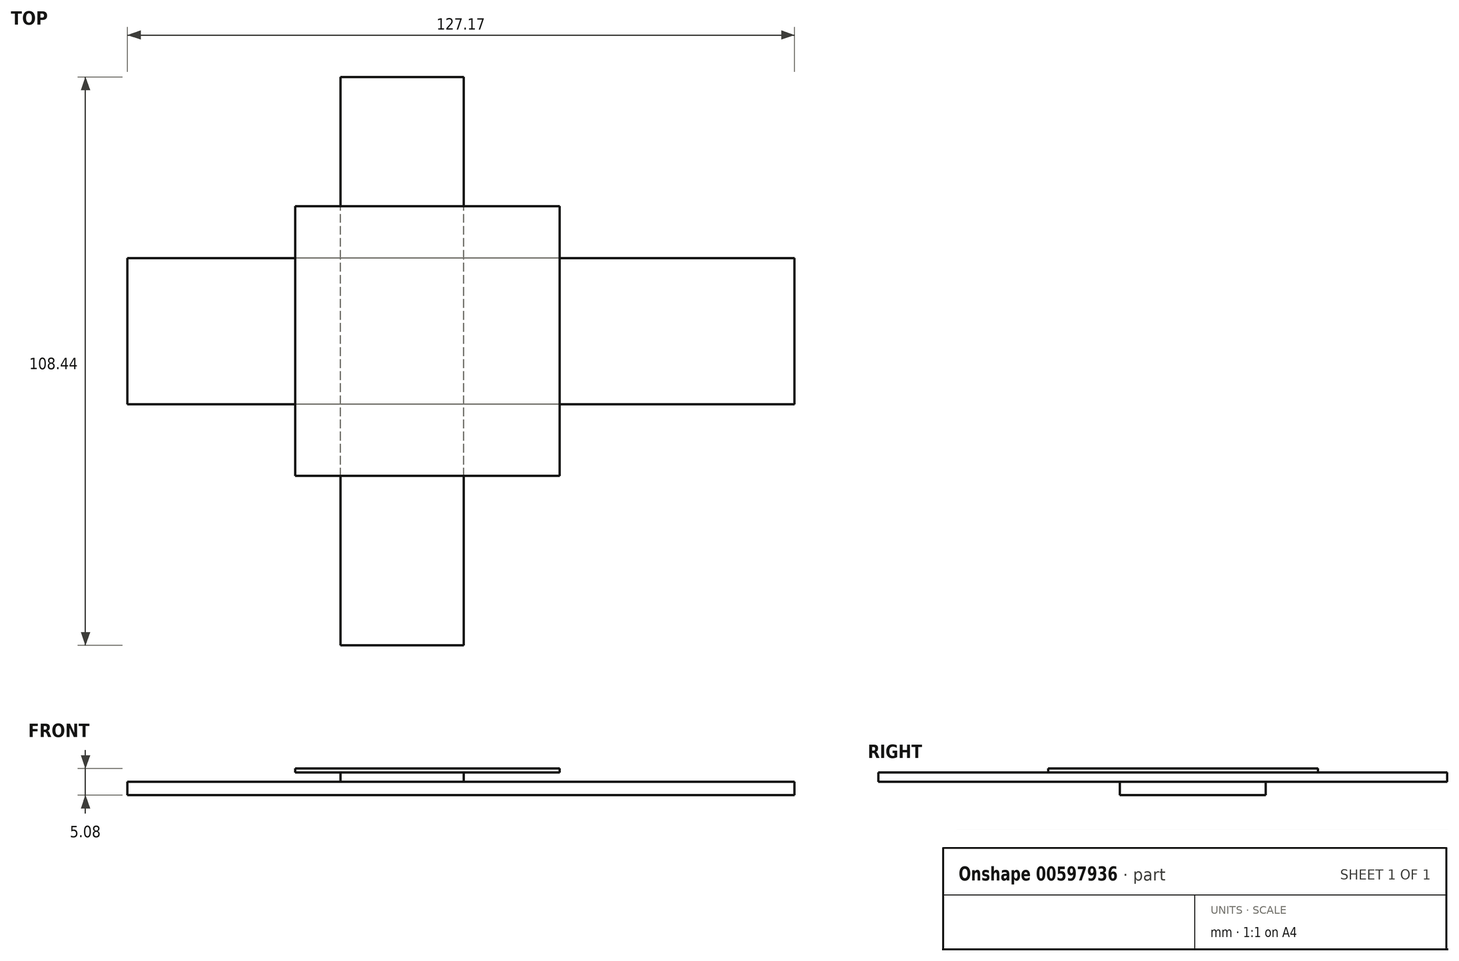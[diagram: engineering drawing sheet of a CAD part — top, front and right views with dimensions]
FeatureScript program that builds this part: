
annotation { "Feature Type Name" : "Feature", "Feature Type Description" : "" }
export const myFeature = defineFeature(function(context is Context, id is Id, definition is map)
    precondition{}
    {
        {
            var Q0;
            Q0=qCreatedBy(makeId("Top.planeOp"),FACE);
            var sketch = newSketch(context, id + "F0", { "sketchPlane" : qUnion([Q0])});
            skLineSegment(sketch, "E0.bottom", {"start": v(49.35, 0) * mm, "end": v(-77.82, 0) * mm});
            skLineSegment(sketch, "E0.top", {"start": v(49.35, 27.86) * mm, "end": v(-77.82, 27.86) * mm});
            skLineSegment(sketch, "E0.left", {"start": v(49.35, 0) * mm, "end": v(49.35, 27.86) * mm});
            skLineSegment(sketch, "E0.right", {"start": v(-77.82, 0) * mm, "end": v(-77.82, 27.86) * mm});
            skPoint(sketch, "E0.middle", {"position": v(-14.24, 13.93) * mm});
            skSolve(sketch);
        }
        {
            var Q0;
            Q0 = qSketchRegion(id + "F0", true);
            extrude(context, id + "F1", {"entities" : qUnion([Q0]), "depth" : 2.54 * mm, "offsetDistance" : 25.4 * mm});
        }
        {
            var Q0;
            Q0=makeQuery(id+"F1.opExtrude","CAP_FACE",FACE,{"disambiguationData":[OSD([sQuery(id+"F0.wireOp",EDGE,"E0.bottom"),sQuery(id+"F0.wireOp",EDGE,"E0.top"),sQuery(id+"F0.wireOp",EDGE,"E0.left"),sQuery(id+"F0.wireOp",EDGE,"E0.right")])],"isStart":false});
            var sketch = newSketch(context, id + "F2", { "sketchPlane" : qUnion([Q0])});
            skLineSegment(sketch, "E1.bottom", {"start": v(-13.68, -46.02) * mm, "end": v(-37.2, -46.02) * mm});
            skLineSegment(sketch, "E1.top", {"start": v(-13.68, 62.42) * mm, "end": v(-37.2, 62.42) * mm});
            skLineSegment(sketch, "E1.left", {"start": v(-13.68, -46.02) * mm, "end": v(-13.68, 62.42) * mm});
            skLineSegment(sketch, "E1.right", {"start": v(-37.2, -46.02) * mm, "end": v(-37.2, 62.42) * mm});
            skPoint(sketch, "E1.middle", {"position": v(-25.43, 8.2) * mm});
            skSolve(sketch);
        }
        {
            var Q0;
            {var subQ0=sQuery(id+"F2.wireOp",EDGE,"E1.left");var subQ1=makeQuery(id+"F1.opExtrude","CAP_EDGE",EDGE,{"disambiguationData":[OSD([sQuery(id+"F0.wireOp",EDGE,"E0.bottom")])],"isStart":false});var subQ2=makeQuery(id+"F2.imprint","INTERSECT",VERTEX,{"derivedFrom":[subQ1,subQ0]});Q0=makeQuery(id+"F2.imprint","IMPRINT",FACE,{"disambiguationData":[TD([[makeQuery(id+"F2.imprint","IMPRINT",EDGE,{"disambiguationData":[TD([[subQ2,-1.0]])],"derivedFrom":subQ0}),1.0]])]});}
            var Q1;
            {var subQ0=sQuery(id+"F2.wireOp",EDGE,"E1.bottom");Q1=makeQuery(id+"F2.imprint","IMPRINT",FACE,{"disambiguationData":[TD([[makeQuery(id+"F2.imprint","IMPRINT",EDGE,{"derivedFrom":subQ0}),-1.0]])]});}
            var Q2;
            {var subQ0=sQuery(id+"F2.wireOp",EDGE,"E1.top");Q2=makeQuery(id+"F2.imprint","IMPRINT",FACE,{"disambiguationData":[TD([[makeQuery(id+"F2.imprint","IMPRINT",EDGE,{"derivedFrom":subQ0}),1.0]])]});}
            extrude(context, id + "F3", {"entities" : qUnion([Q0, Q1, Q2]), "operationType" : NewBodyOperationType.ADD, "depth" : 1.78 * mm, "offsetDistance" : 25.4 * mm});
        }
        {
            var Q0;
            Q0=makeQuery(id+"F3.opExtrude","CAP_FACE",FACE,{"disambiguationData":[OSD([sQuery(id+"F2.wireOp",EDGE,"E1.bottom"),sQuery(id+"F2.wireOp",EDGE,"E1.top"),sQuery(id+"F2.wireOp",EDGE,"E1.left"),sQuery(id+"F2.wireOp",EDGE,"E1.right")])],"isStart":false});
            var sketch = newSketch(context, id + "F4", { "sketchPlane" : qUnion([Q0])});
            skLineSegment(sketch, "E2.bottom", {"start": v(4.58, -13.66) * mm, "end": v(-45.84, -13.66) * mm});
            skLineSegment(sketch, "E2.top", {"start": v(4.58, 37.78) * mm, "end": v(-45.84, 37.78) * mm});
            skLineSegment(sketch, "E2.left", {"start": v(4.58, -13.66) * mm, "end": v(4.58, 37.78) * mm});
            skLineSegment(sketch, "E2.right", {"start": v(-45.84, -13.66) * mm, "end": v(-45.84, 37.78) * mm});
            skPoint(sketch, "E2.middle", {"position": v(-20.63, 12.06) * mm});
            skSolve(sketch);
        }
        {
            var Q0;
            {var subQ0=sQuery(id+"F4.wireOp",EDGE,"E2.left");Q0=makeQuery(id+"F4.imprint","IMPRINT",FACE,{"disambiguationData":[TD([[makeQuery(id+"F4.imprint","IMPRINT",EDGE,{"derivedFrom":subQ0}),1.0]])]});}
            var Q1;
            {var subQ0=sQuery(id+"F4.wireOp",EDGE,"E2.bottom");var subQ1=makeQuery(id+"F3.opExtrude","CAP_EDGE",EDGE,{"disambiguationData":[OSD([sQuery(id+"F2.wireOp",EDGE,"E1.left")])],"isStart":false});var subQ2=makeQuery(id+"F4.imprint","INTERSECT",VERTEX,{"derivedFrom":[subQ1,subQ0]});Q1=makeQuery(id+"F4.imprint","IMPRINT",FACE,{"disambiguationData":[TD([[makeQuery(id+"F4.imprint","IMPRINT",EDGE,{"disambiguationData":[TD([[subQ2,-1.0]])],"derivedFrom":subQ0}),-1.0]])]});}
            var Q2;
            {var subQ0=sQuery(id+"F4.wireOp",EDGE,"E2.right");Q2=makeQuery(id+"F4.imprint","IMPRINT",FACE,{"disambiguationData":[TD([[makeQuery(id+"F4.imprint","IMPRINT",EDGE,{"derivedFrom":subQ0}),-1.0]])]});}
            extrude(context, id + "F5", {"entities" : qUnion([Q0, Q1, Q2]), "operationType" : NewBodyOperationType.ADD, "depth" : 0.76 * mm, "offsetDistance" : 25.4 * mm});
        }
    });
